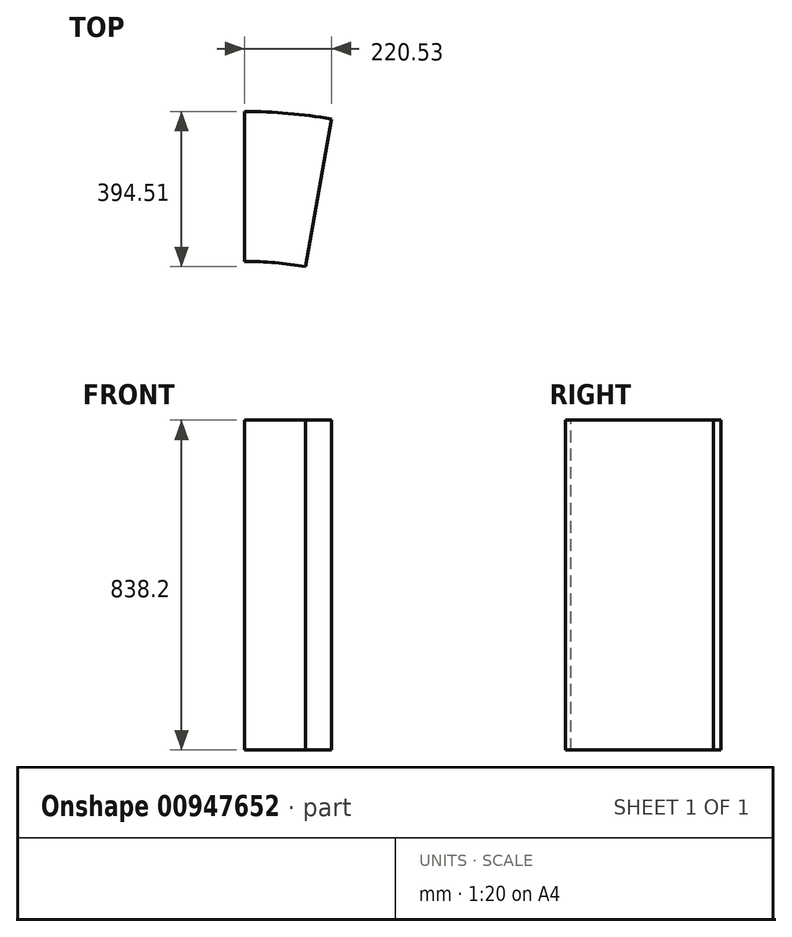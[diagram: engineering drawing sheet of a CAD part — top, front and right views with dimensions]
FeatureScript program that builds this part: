
annotation { "Feature Type Name" : "Feature", "Feature Type Description" : "" }
export const myFeature = defineFeature(function(context is Context, id is Id, definition is map)
    precondition{}
    {
        {
            var Q0;
            Q0=qCreatedBy(makeId("Top.planeOp"),FACE);
            var sketch = newSketch(context, id + "F0", { "sketchPlane" : qUnion([Q0])});
            skCircle(sketch, "E0", {"center": v(0, 0) * mm, "radius": 1270 * mm});
            skCircle(sketch, "E1", {"center": v(0, 0) * mm, "radius": 889 * mm});
            skSolve(sketch);
        }
        {
            var Q0;
            Q0=qCreatedBy(makeId("Top.planeOp"),FACE);
            var sketch = newSketch(context, id + "F1", { "sketchPlane" : qUnion([Q0])});
            skArc(sketch, "E2.0", {"start": v(220.53, 1250.7) * mm, "mid": v(110.69, 1265.17) * mm, "end": v(0, 1270) * mm});
            skArc(sketch, "E3.0", {"start": v(154.37, 875.5) * mm, "mid": v(77.48, 885.62) * mm, "end": v(0, 889) * mm});
            skLineSegment(sketch, "E4", {"start": v(0, 1270) * mm, "end": v(0, 889) * mm});
            skLineSegment(sketch, "E5", {"start": v(154.37, 875.5) * mm, "end": v(220.53, 1250.7) * mm});
            skSolve(sketch);
        }
        {
            var Q0;
            Q0 = qSketchRegion(id + "F1", true);
            extrude(context, id + "F2", {"entities" : qUnion([Q0]), "oppositeDirection" : true, "depth" : 838.2 * mm, "offsetDistance" : 25.4 * mm});
        }
    });
